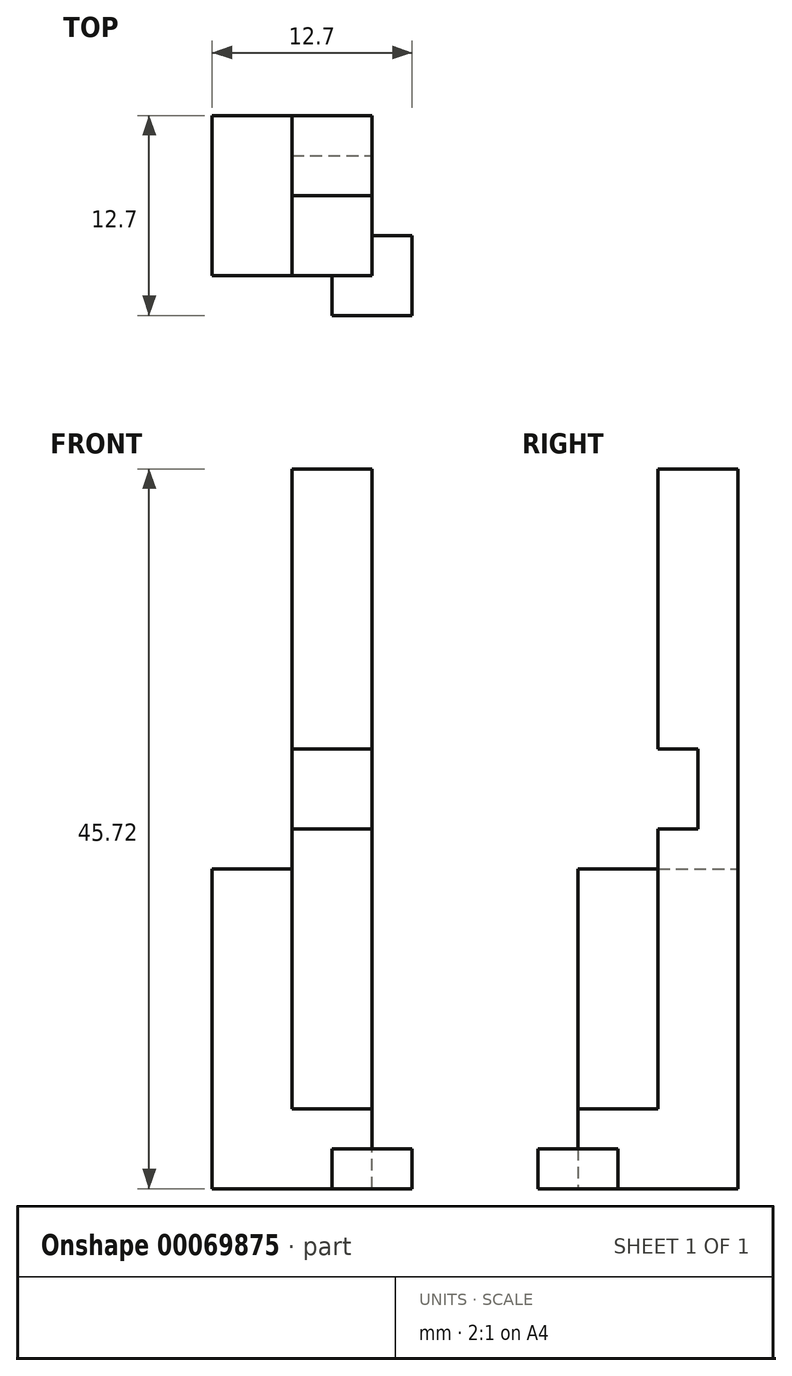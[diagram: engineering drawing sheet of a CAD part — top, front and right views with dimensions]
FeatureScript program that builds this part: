
annotation { "Feature Type Name" : "Feature", "Feature Type Description" : "" }
export const myFeature = defineFeature(function(context is Context, id is Id, definition is map)
    precondition{}
    {
        {
            var Q0;
            Q0=qCreatedBy(makeId("Top.planeOp"),FACE);
            var sketch = newSketch(context, id + "F0", { "sketchPlane" : qUnion([Q0])});
            skLineSegment(sketch, "E0.bottom", {"start": v(0, 0) * mm, "end": v(10.16, 0) * mm});
            skLineSegment(sketch, "E0.top", {"start": v(0, -10.16) * mm, "end": v(10.16, -10.16) * mm});
            skLineSegment(sketch, "E0.left", {"start": v(0, 0) * mm, "end": v(0, -10.16) * mm});
            skLineSegment(sketch, "E0.right", {"start": v(10.16, 0) * mm, "end": v(10.16, -10.16) * mm});
            skSolve(sketch);
        }
        {
            var Q0;
            Q0 = qSketchRegion(id + "F0", true);
            extrude(context, id + "F1", {"entities" : qUnion([Q0]), "depth" : 5.08 * mm});
        }
        {
            var Q0;
            Q0=makeQuery(id+"F1.opExtrude","CAP_FACE",FACE,{"disambiguationData":[OSD([sQuery(id+"F0.wireOp",EDGE,"E0.bottom"),sQuery(id+"F0.wireOp",EDGE,"E0.top"),sQuery(id+"F0.wireOp",EDGE,"E0.left"),sQuery(id+"F0.wireOp",EDGE,"E0.right")])],"isStart":true});
            var sketch = newSketch(context, id + "F2", { "sketchPlane" : qUnion([Q0])});
            skLineSegment(sketch, "E1.bottom", {"start": v(7.62, 7.62) * mm, "end": v(12.7, 7.62) * mm});
            skLineSegment(sketch, "E1.top", {"start": v(7.62, 12.7) * mm, "end": v(12.7, 12.7) * mm});
            skLineSegment(sketch, "E1.left", {"start": v(7.62, 7.62) * mm, "end": v(7.62, 12.7) * mm});
            skLineSegment(sketch, "E1.right", {"start": v(12.7, 7.62) * mm, "end": v(12.7, 12.7) * mm});
            skSolve(sketch);
        }
        {
            var Q0;
            Q0 = qSketchRegion(id + "F2", true);
            extrude(context, id + "F3", {"entities" : qUnion([Q0]), "operationType" : NewBodyOperationType.ADD, "oppositeDirection" : true, "depth" : 2.54 * mm});
        }
        {
            var Q0;
            Q0=makeQuery(id+"F1.opExtrude","CAP_FACE",FACE,{"disambiguationData":[OSD([sQuery(id+"F0.wireOp",EDGE,"E0.bottom"),sQuery(id+"F0.wireOp",EDGE,"E0.top"),sQuery(id+"F0.wireOp",EDGE,"E0.left"),sQuery(id+"F0.wireOp",EDGE,"E0.right")])],"isStart":false});
            var sketch = newSketch(context, id + "F4", { "sketchPlane" : qUnion([Q0])});
            skLineSegment(sketch, "E2.bottom", {"start": v(10.16, 0) * mm, "end": v(5.08, 0) * mm});
            skLineSegment(sketch, "E2.top", {"start": v(10.16, -5.08) * mm, "end": v(5.08, -5.08) * mm});
            skLineSegment(sketch, "E2.left", {"start": v(10.16, 0) * mm, "end": v(10.16, -5.08) * mm});
            skLineSegment(sketch, "E2.right", {"start": v(5.08, 0) * mm, "end": v(5.08, -5.08) * mm});
            skSolve(sketch);
        }
        {
            var Q0;
            Q0 = qSketchRegion(id + "F4", true);
            extrude(context, id + "F5", {"entities" : qUnion([Q0]), "operationType" : NewBodyOperationType.ADD, "depth" : 40.64 * mm});
        }
        {
            var Q0;
            Q0=makeQuery(id+"F5.boolean.opBoolean","MERGE",FACE,{"derivedFrom":[makeQuery(id+"F1.opExtrude","SWEPT_FACE",FACE,{"disambiguationData":[OSD([sQuery(id+"F0.wireOp",EDGE,"E0.right")])]}),makeQuery(id+"F5.opExtrude","SWEPT_FACE",FACE,{"disambiguationData":[OSD([sQuery(id+"F4.wireOp",EDGE,"E2.left")])]})]});
            var sketch = newSketch(context, id + "F6", { "sketchPlane" : qUnion([Q0])});
            skLineSegment(sketch, "E3.bottom", {"start": v(-2.54, 22.86) * mm, "end": v(-7.62, 22.86) * mm});
            skLineSegment(sketch, "E3.top", {"start": v(-2.54, 27.94) * mm, "end": v(-7.62, 27.94) * mm});
            skLineSegment(sketch, "E3.left", {"start": v(-2.54, 22.86) * mm, "end": v(-2.54, 27.94) * mm});
            skLineSegment(sketch, "E3.right", {"start": v(-7.62, 22.86) * mm, "end": v(-7.62, 27.94) * mm});
            skSolve(sketch);
        }
        {
            var Q0;
            Q0 = qSketchRegion(id + "F6", true);
            extrude(context, id + "F7", {"entities" : qUnion([Q0]), "operationType" : NewBodyOperationType.REMOVE, "oppositeDirection" : true, "depth" : 25.4 * mm});
        }
        {
            var Q0;
            Q0=makeQuery(id+"F1.opExtrude","CAP_FACE",FACE,{"disambiguationData":[OSD([sQuery(id+"F0.wireOp",EDGE,"E0.bottom"),sQuery(id+"F0.wireOp",EDGE,"E0.top"),sQuery(id+"F0.wireOp",EDGE,"E0.left"),sQuery(id+"F0.wireOp",EDGE,"E0.right")])],"isStart":false});
            var sketch = newSketch(context, id + "F8", { "sketchPlane" : qUnion([Q0])});
            skLineSegment(sketch, "E4.bottom", {"start": v(10.16, -10.16) * mm, "end": v(5.08, -10.16) * mm});
            skLineSegment(sketch, "E4.top", {"start": v(10.16, -5.08) * mm, "end": v(5.08, -5.08) * mm});
            skLineSegment(sketch, "E4.left", {"start": v(10.16, -10.16) * mm, "end": v(10.16, -5.08) * mm});
            skLineSegment(sketch, "E4.right", {"start": v(5.08, -10.16) * mm, "end": v(5.08, -5.08) * mm});
            skSolve(sketch);
        }
        {
            var Q0;
            {var subQ2=sQuery(id+"F8.wireOp",EDGE,"E4.right");Q0=makeQuery(id+"F8.imprint","IMPRINT",FACE,{"disambiguationData":[TD([[makeQuery(id+"F8.imprint","IMPRINT",EDGE,{"derivedFrom":subQ2}),1.0]])]});}
            var sketch = newSketch(context, id + "F9", { "sketchPlane" : qUnion([Q0])});
            skLineSegment(sketch, "E5.bottom", {"start": v(0, 0) * mm, "end": v(5.08, 0) * mm});
            skLineSegment(sketch, "E5.top", {"start": v(0, -10.16) * mm, "end": v(5.08, -10.16) * mm});
            skLineSegment(sketch, "E5.left", {"start": v(0, 0) * mm, "end": v(0, -10.16) * mm});
            skLineSegment(sketch, "E5.right", {"start": v(5.08, 0) * mm, "end": v(5.08, -10.16) * mm});
            skSolve(sketch);
        }
        {
            var Q0;
            Q0 = qSketchRegion(id + "F9", true);
            extrude(context, id + "F10", {"entities" : qUnion([Q0]), "operationType" : NewBodyOperationType.ADD, "depth" : 15.24 * mm});
        }
    });
